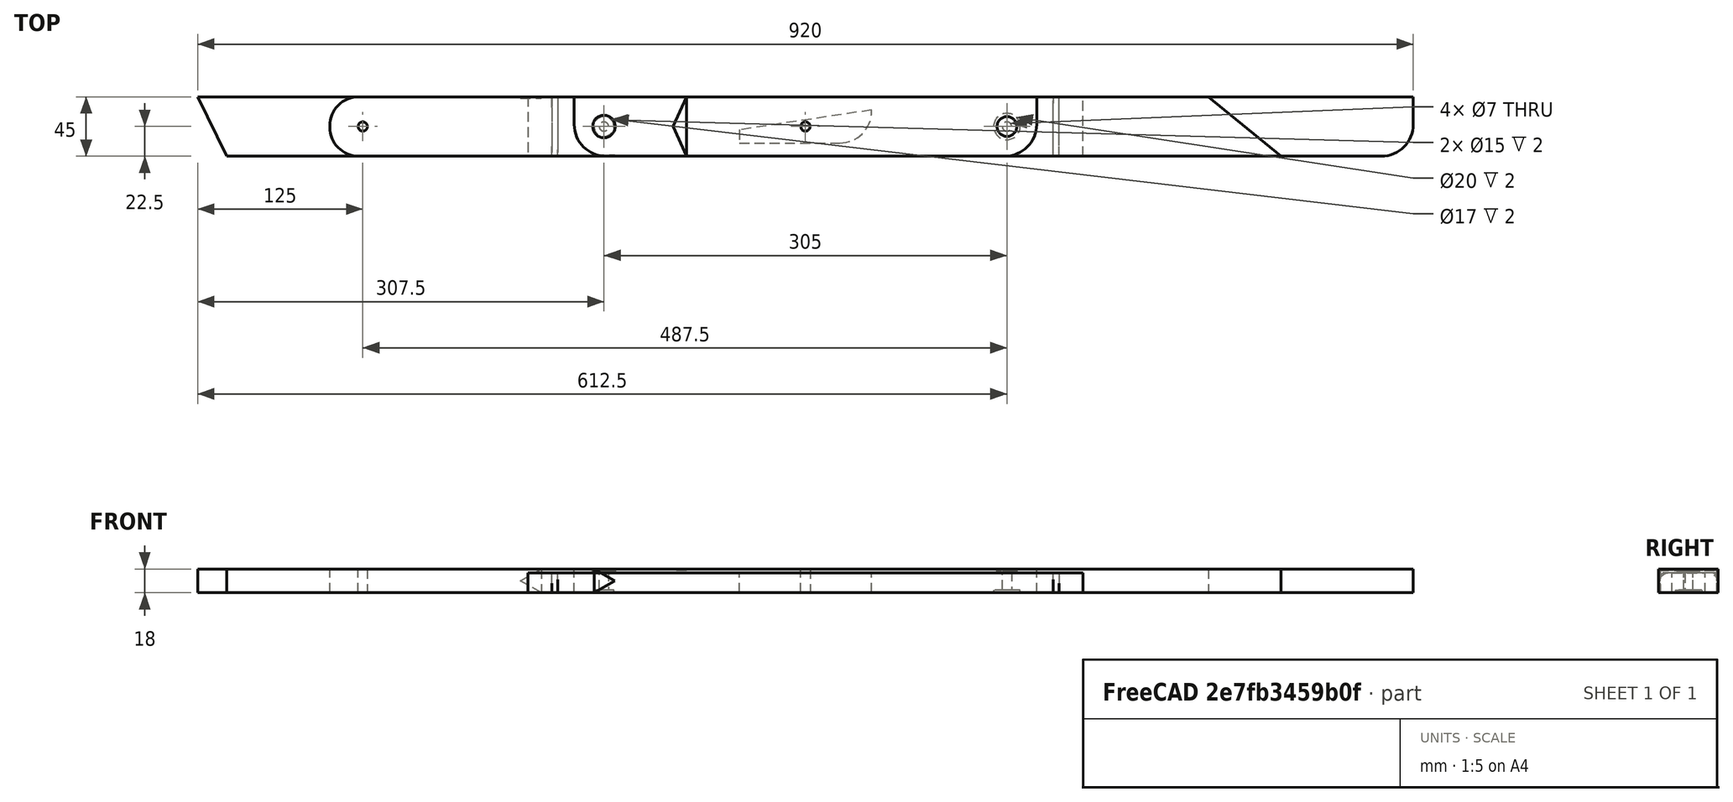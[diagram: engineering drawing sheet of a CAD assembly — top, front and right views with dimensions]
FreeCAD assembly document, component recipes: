
FREECAD ASSEMBLY — COMPONENT RECIPES ("montagem_final")

This assembly document has 20 components, labeled P0..P19 below (a component is one placed body or linked part). 20 of them carry a construction recipe — the FreeCAD feature program that regenerates the part from scratch, quoted from this document or its linked companion documents; the rest are supplied as boundary geometry only. No exploded tour is included for this assembly.
COMPONENT P0 — recipe-attached ("35 X 4,5 X 1,8 (1)", modeled in this document).
Construction recipe (the document's own serialized feature program — sketch geometry with constraints, then the solid features built on it; lengths are millimeters unless a unit is written):

FEATURE [Sketcher::SketchObject] Sketch
  FullyConstrained = true
  MapMode = 5
  Support = -> [XY_Plane]
  sketch-geometry (5):
    g0: LineSegment StartX=-175 StartY=22.5 StartZ=0 EndX=-175 EndY=-22.5 EndZ=0
    g1: LineSegment StartX=-175 StartY=-22.5 StartZ=0 EndX=175 EndY=-22.5 EndZ=0
    g2: LineSegment StartX=175 StartY=-22.5 StartZ=0 EndX=175 EndY=22.5 EndZ=0
    g3: LineSegment StartX=175 StartY=22.5 StartZ=0 EndX=-175 EndY=22.5 EndZ=0
    g4: GeomPoint X=0 Y=0 Z=0
  constraints (12):
    c: Coincident(g0,g1)
    c: Coincident(g1,g2)
    c: Coincident(g2,g3)
    c: Coincident(g3,g0)
    c: Horizontal(g1)
    c: Horizontal(g3)
    c: Vertical(g0)
    c: Vertical(g2)
    c: Symmetric(g1,g0,g4)
    c: Coincident(g4,g-1)
    c: DistanceY(g0,g0) = 45
    c: DistanceX(g3,g3) = 350
FEATURE [PartDesign::Pad] Pad
  Direction = (0,0,1)
  Length = 18
  Length2 = 10
  Profile = -> Sketch
  ReferenceAxis = -> Sketch [N_Axis]
  Type = 0
FEATURE [Sketcher::SketchObject] Sketch001
  ExternalGeometry = -> [Pad]
  FullyConstrained = true
  MapMode = 5
  Placement = pos=(0,0,18) rot=(0,0,1;0rad)
  Support = -> [Pad]
  sketch-geometry (2):
    g0: Circle CenterX=-152.5 CenterY=0 CenterZ=0 NormalX=0 NormalY=0 NormalZ=1 AngleXU=0 Radius=3.5
    g1: Circle CenterX=-152.5 CenterY=0 CenterZ=0 NormalX=0 NormalY=0 NormalZ=1 AngleXU=0 Radius=8.5
  constraints (5):
    c: PointOnObject(g0,g-1)
    c: Diameter(g0) = 7
    c: DistanceX(g-3,g0) = 22.5
    c: Coincident(g1,g0)
    c: Diameter(g1) = 17
FEATURE [PartDesign::Pocket] Pocket
  BaseFeature = -> Pad
  Direction = (0,0,-1)
  Length = 2
  Length2 = 5
  Profile = -> Sketch001
  ReferenceAxis = -> Sketch001 [N_Axis]
  Type = 0
FEATURE [PartDesign::Pocket] Pocket001
  BaseFeature = -> Pocket
  Direction = (0,0,-1)
  Length = 5
  Length2 = 5
  Profile = -> Pocket [Edge18]
  Type = 1
FEATURE [PartDesign::LinearPattern] LinearPattern
  BaseFeature = -> Pocket001
  Direction = -> X_Axis
  Length = 305
  Occurrences = 2
  Originals = -> [Pocket001]
FEATURE [Sketcher::SketchObject] Sketch002
  ExternalGeometry = -> [LinearPattern]
  FullyConstrained = true
  MapMode = 5
  Placement = pos=(0,0,0) rot=(1,0,0;3.14159rad)
  Support = -> [LinearPattern]
  sketch-geometry (1):
    g0: Circle CenterX=152.5 CenterY=0 CenterZ=0 NormalX=0 NormalY=0 NormalZ=1 AngleXU=0 Radius=10
  constraints (2):
    c: Coincident(g0,g-3)
    c: Diameter(g0) = 20
FEATURE [PartDesign::Pocket] Pocket002
  BaseFeature = -> LinearPattern
  Direction = (0,0,1)
  Length = 2
  Length2 = 5
  Profile = -> Sketch002
  ReferenceAxis = -> Sketch002 [N_Axis]
  Type = 0
FEATURE [PartDesign::Fillet] Fillet
  Base = -> Pocket002 [Edge2,Edge8]
  BaseFeature = -> Pocket002
  Radius = 24
  SupportTransform = false
  UseAllEdges = false
FEATURE [Sketcher::SketchObject] Sketch003
  ExternalGeometry = -> [Fillet]
  FullyConstrained = true
  MapMode = 5
  Placement = pos=(0,0,18) rot=(0,0,1;0rad)
  Support = -> [Fillet]
  sketch-geometry (1):
    g0: Circle CenterX=152.5 CenterY=0 CenterZ=0 NormalX=0 NormalY=0 NormalZ=1 AngleXU=0 Radius=7.5
  constraints (2):
    c: Coincident(g0,g-3)
    c: Diameter(g0) = 15
FEATURE [PartDesign::Pocket] Pocket003
  BaseFeature = -> Fillet
  Direction = (0,0,-1)
  Length = 2
  Length2 = 5
  Profile = -> Sketch003
  ReferenceAxis = -> Sketch003 [N_Axis]
  Type = 0
FEATURE [Sketcher::SketchObject] Sketch004
  ExternalGeometry = -> [Pocket003]
  FullyConstrained = true
  MapMode = 5
  Placement = pos=(0,0,0) rot=(1,0,0;3.14159rad)
  Support = -> [Pocket003]
  sketch-geometry (1):
    g0: Circle CenterX=-152.5 CenterY=0 CenterZ=0 NormalX=0 NormalY=0 NormalZ=1 AngleXU=0 Radius=7.5
  constraints (2):
    c: Coincident(g0,g-3)
    c: Diameter(g0) = 15
FEATURE [PartDesign::Pocket] Pocket004
  BaseFeature = -> Pocket003
  Direction = (0,0,1)
  Length = 2
  Length2 = 5
  Profile = -> Sketch004
  ReferenceAxis = -> Sketch004 [N_Axis]
  Type = 0
FEATURE [PartDesign::Body] Body  label="35 x 4,5 x 1,8"
  Group = -> [Sketch,Pad,Sketch001,Pocket,Pocket001,LinearPattern,Sketch002,Pocket002,Fillet,Sketch003,Pocket003,Sketch004,Pocket004]
  Origin = -> Origin
  Tip = -> Pocket004
COMPONENT P1 — recipe-attached ("37,5 X 4,5 X 1,5 (1)", modeled in this document).
Construction recipe (the document's own serialized feature program — sketch geometry with constraints, then the solid features built on it; lengths are millimeters unless a unit is written):

FEATURE [Sketcher::SketchObject] Sketch005
  FullyConstrained = true
  MapMode = 5
  Support = -> [XY_Plane001]
  sketch-geometry (5):
    g0: LineSegment StartX=-187.5 StartY=22.5 StartZ=0 EndX=-187.5 EndY=-22.5 EndZ=0
    g1: LineSegment StartX=-187.5 StartY=-22.5 StartZ=0 EndX=187.5 EndY=-22.5 EndZ=0
    g2: LineSegment StartX=187.5 StartY=-22.5 StartZ=0 EndX=187.5 EndY=22.5 EndZ=0
    g3: LineSegment StartX=187.5 StartY=22.5 StartZ=0 EndX=-187.5 EndY=22.5 EndZ=0
    g4: GeomPoint X=0 Y=0 Z=0
  constraints (12):
    c: Coincident(g0,g1)
    c: Coincident(g1,g2)
    c: Coincident(g2,g3)
    c: Coincident(g3,g0)
    c: Horizontal(g1)
    c: Horizontal(g3)
    c: Vertical(g0)
    c: Vertical(g2)
    c: Symmetric(g1,g0,g4)
    c: Coincident(g4,g-1)
    c: DistanceY(g0,g0) = 45
    c: DistanceX(g3,g3) = 375
FEATURE [PartDesign::Pad] Pad001
  Direction = (0,0,1)
  Length = 15
  Length2 = 10
  Profile = -> Sketch005
  ReferenceAxis = -> Sketch005 [N_Axis]
  Type = 0
FEATURE [PartDesign::Fillet] Fillet001
  Base = -> Pad001 [Edge7,Edge12]
  BaseFeature = -> Pad001
  Radius = 5
  SupportTransform = false
  UseAllEdges = false
FEATURE [PartDesign::Body] Body001  label="37,5 x 4,5 x 1,5"
  Group = -> [Sketch005,Pad001,Fillet001]
  Origin = -> Origin001
  Tip = -> Fillet001
COMPONENT P2 — same part as P1; its construction recipe is shown at P1.
COMPONENT P3 — same part as P0; its construction recipe is shown at P0.
COMPONENT P4 — same part as P1; its construction recipe is shown at P1.
COMPONENT P5 — same part as P1; its construction recipe is shown at P1.
COMPONENT P6 — same part as P1; its construction recipe is shown at P1.
COMPONENT P7 — same part as P1; its construction recipe is shown at P1.
COMPONENT P8 — same part as P1; its construction recipe is shown at P1.
COMPONENT P9 — recipe-attached ("pe1", modeled in this document).
Construction recipe (the document's own serialized feature program — sketch geometry with constraints, then the solid features built on it; lengths are millimeters unless a unit is written):

FEATURE [Sketcher::SketchObject] Sketch006
  FullyConstrained = true
  MapMode = 5
  Support = -> [XY_Plane002]
  sketch-geometry (5):
    g0: LineSegment StartX=-360 StartY=22.5 StartZ=0 EndX=-360 EndY=-22.5 EndZ=0
    g1: LineSegment StartX=-360 StartY=-22.5 StartZ=0 EndX=360 EndY=-22.5 EndZ=0
    g2: LineSegment StartX=360 StartY=-22.5 StartZ=0 EndX=360 EndY=22.5 EndZ=0
    g3: LineSegment StartX=360 StartY=22.5 StartZ=0 EndX=-360 EndY=22.5 EndZ=0
    g4: GeomPoint X=0 Y=0 Z=0
  constraints (12):
    c: Coincident(g0,g1)
    c: Coincident(g1,g2)
    c: Coincident(g2,g3)
    c: Coincident(g3,g0)
    c: Horizontal(g1)
    c: Horizontal(g3)
    c: Vertical(g0)
    c: Vertical(g2)
    c: Symmetric(g1,g0,g4)
    c: Coincident(g4,g-1)
    c: DistanceY(g2,g2) = 45
    c: DistanceX(g3,g3) = 720
FEATURE [PartDesign::Pad] Pad002
  Direction = (0,0,1)
  Length = 18
  Length2 = 10
  Profile = -> Sketch006
  ReferenceAxis = -> Sketch006 [N_Axis]
  Type = 0
FEATURE [Sketcher::SketchObject] Sketch007
  ExternalGeometry = -> [Pad002]
  FullyConstrained = true
  MapMode = 5
  Placement = pos=(0,0,18) rot=(0,0,1;0rad)
  Support = -> [Pad002]
  sketch-geometry (1):
    g0: Circle CenterX=-335 CenterY=0 CenterZ=0 NormalX=0 NormalY=0 NormalZ=1 AngleXU=0 Radius=3.5
  constraints (3):
    c: PointOnObject(g0,g-1)
    c: Diameter(g0) = 7
    c: DistanceX(g-3,g0) = 25
FEATURE [PartDesign::Pocket] Pocket006
  BaseFeature = -> Pad002
  Direction = (0,0,-1)
  Length = 5
  Length2 = 5
  Profile = -> Sketch007
  ReferenceAxis = -> Sketch007 [N_Axis]
  Type = 1
FEATURE [PartDesign::Fillet] Fillet002
  Base = -> Pocket006 [Edge2,Edge1]
  BaseFeature = -> Pocket006
  Radius = 22
  SupportTransform = false
  UseAllEdges = false
FEATURE [Sketcher::SketchObject] Sketch008
  ExternalGeometry = -> [Fillet002]
  FullyConstrained = true
  MapMode = 5
  Placement = pos=(0,0,18) rot=(0,0,1;0rad)
  Support = -> [Fillet002]
  sketch-geometry (3):
    g0: LineSegment StartX=-90 StartY=-22.5 StartZ=0 EndX=-90 EndY=22.5 EndZ=0
    g1: LineSegment StartX=-90 StartY=22.5 StartZ=0 EndX=-100 EndY=0 EndZ=0
    g2: LineSegment StartX=-100 StartY=0 StartZ=0 EndX=-90 EndY=-22.5 EndZ=0
  constraints (9):
    c: PointOnObject(g0,g-3)
    c: PointOnObject(g0,g-4)
    c: Vertical(g0)
    c: Coincident(g0,g1)
    c: PointOnObject(g1,g-1)
    c: Coincident(g1,g2)
    c: Coincident(g2,g0)
    c: DistanceX(g-5,g0) = 270
    c: DistanceX(g1,g0) = 10
FEATURE [PartDesign::Pocket] Pocket007
  BaseFeature = -> Fillet002
  Direction = (0,0,-1)
  Length = 1
  Length2 = 5
  Profile = -> Sketch008
  ReferenceAxis = -> Sketch008 [N_Axis]
  Type = 0
FEATURE [Sketcher::SketchObject] Sketch009
  ExternalGeometry = -> [Pocket007]
  FullyConstrained = true
  MapMode = 5
  Placement = pos=(0,0,18) rot=(0,0,1;0rad)
  Support = -> [Pocket007]
  sketch-geometry (3):
    g0: LineSegment StartX=360 StartY=22.5 StartZ=0 EndX=305 EndY=22.5 EndZ=0
    g1: LineSegment StartX=305 StartY=22.5 StartZ=0 EndX=360 EndY=-22.5 EndZ=0
    g2: LineSegment StartX=360 StartY=22.5 StartZ=0 EndX=360 EndY=-22.5 EndZ=0
  constraints (7):
    c: Coincident(g-4,g0)
    c: PointOnObject(g0,g-3)
    c: Coincident(g0,g1)
    c: Coincident(g1,g-4)
    c: DistanceX(g0,g0) = 55
    c: Coincident(g2,g0)
    c: Coincident(g2,g1)
FEATURE [PartDesign::Pocket] Pocket005
  BaseFeature = -> Pocket007
  Direction = (0,0,-1)
  Length = 5
  Length2 = 5
  Profile = -> Sketch009
  ReferenceAxis = -> Sketch009 [N_Axis]
  Type = 1
FEATURE [PartDesign::Body] Body002  label="72 x 4,5 x 1,8"
  Group = -> [Sketch006,Pad002,Sketch007,Pocket006,Fillet002,Sketch008,Pocket007,Sketch009,Pocket005]
  Origin = -> Origin002
  Tip = -> Pocket005
COMPONENT P10 — same part as P9; its construction recipe is shown at P9.
COMPONENT P11 — same part as P1; its construction recipe is shown at P1.
COMPONENT P12 — recipe-attached ("92 X 4,5 X 1,8 (1)", modeled in this document).
Construction recipe (the document's own serialized feature program — sketch geometry with constraints, then the solid features built on it; lengths are millimeters unless a unit is written):

FEATURE [Sketcher::SketchObject] Sketch010
  FullyConstrained = true
  MapMode = 5
  Support = -> [XY_Plane003]
  sketch-geometry (5):
    g0: LineSegment StartX=-460 StartY=22.5 StartZ=0 EndX=-460 EndY=-22.5 EndZ=0
    g1: LineSegment StartX=-460 StartY=-22.5 StartZ=0 EndX=460 EndY=-22.5 EndZ=0
    g2: LineSegment StartX=460 StartY=-22.5 StartZ=0 EndX=460 EndY=22.5 EndZ=0
    g3: LineSegment StartX=460 StartY=22.5 StartZ=0 EndX=-460 EndY=22.5 EndZ=0
    g4: GeomPoint X=0 Y=0 Z=0
  constraints (12):
    c: Coincident(g0,g1)
    c: Coincident(g1,g2)
    c: Coincident(g2,g3)
    c: Coincident(g3,g0)
    c: Horizontal(g1)
    c: Horizontal(g3)
    c: Vertical(g0)
    c: Vertical(g2)
    c: Symmetric(g1,g0,g4)
    c: Coincident(g4,g-1)
    c: DistanceY(g2,g2) = 45
    c: DistanceX(g3,g3) = 920
FEATURE [PartDesign::Pad] Pad003
  Direction = (0,0,1)
  Length = 18
  Length2 = 10
  Profile = -> Sketch010
  ReferenceAxis = -> Sketch010 [N_Axis]
  Type = 0
FEATURE [Sketcher::SketchObject] Sketch011
  FullyConstrained = true
  MapMode = 5
  Placement = pos=(0,0,18) rot=(0,0,1;0rad)
  Support = -> [Pad003]
  sketch-geometry (1):
    g0: Circle CenterX=0 CenterY=0 CenterZ=0 NormalX=0 NormalY=0 NormalZ=1 AngleXU=0 Radius=3.5
  constraints (2):
    c: Coincident(g0,g-1)
    c: Diameter(g0) = 7
FEATURE [PartDesign::Pocket] Pocket009
  BaseFeature = -> Pad003
  Direction = (0,0,-1)
  Length = 5
  Length2 = 5
  Profile = -> Sketch011
  ReferenceAxis = -> Sketch011 [N_Axis]
  Type = 1
FEATURE [PartDesign::Fillet] Fillet003
  Base = -> Pocket009 [Edge8]
  BaseFeature = -> Pocket009
  Radius = 24
  SupportTransform = false
  UseAllEdges = false
FEATURE [Sketcher::SketchObject] Sketch012
  ExternalGeometry = -> [Fillet003]
  FullyConstrained = true
  MapMode = 5
  Placement = pos=(0,-22.5,0) rot=(1,0,0;1.5708rad)
  Support = -> [Fillet003]
  sketch-geometry (3):
    g0: LineSegment StartX=-160 StartY=18 StartZ=0 EndX=-160 EndY=0 EndZ=0
    g1: LineSegment StartX=-160 StartY=0 StartZ=0 EndX=-144.412 EndY=9 EndZ=0
    g2: LineSegment StartX=-144.412 StartY=9 StartZ=0 EndX=-160 EndY=18 EndZ=0
  constraints (9):
    c: PointOnObject(g0,g-3)
    c: PointOnObject(g0,g-4)
    c: Vertical(g0)
    c: DistanceX(g-3,g0) = 300
    c: Coincident(g0,g1)
    c: Coincident(g1,g2)
    c: Coincident(g2,g0)
    c: Equal(g2,g1)
    c: Equal(g0,g1)
FEATURE [PartDesign::Pocket] Pocket010
  BaseFeature = -> Fillet003
  Direction = (0,1,-2e-16)
  Length = 1
  Length2 = 5
  Profile = -> Sketch012
  ReferenceAxis = -> Sketch012 [N_Axis]
  Type = 0
FEATURE [Sketcher::SketchObject] Sketch013
  ExternalGeometry = -> [Pocket010]
  FullyConstrained = true
  MapMode = 5
  Placement = pos=(0,22.5,0) rot=(0,0.707107,0.707107;3.14159rad)
  Support = -> [Pocket010]
  sketch-geometry (3):
    g0: LineSegment StartX=200 StartY=18 StartZ=0 EndX=200 EndY=0 EndZ=0
    g1: LineSegment StartX=200 StartY=0 StartZ=0 EndX=215.588 EndY=9 EndZ=0
    g2: LineSegment StartX=215.588 StartY=9 StartZ=0 EndX=200 EndY=18 EndZ=0
  constraints (9):
    c: PointOnObject(g0,g-3)
    c: PointOnObject(g0,g-4)
    c: Vertical(g0)
    c: Coincident(g0,g1)
    c: Coincident(g1,g2)
    c: Coincident(g2,g0)
    c: Equal(g0,g2)
    c: Equal(g2,g1)
    c: DistanceX(g0,g-3) = 260
FEATURE [PartDesign::Pocket] Pocket011
  BaseFeature = -> Pocket010
  Direction = (0,-1,2e-16)
  Length = 1
  Length2 = 5
  Profile = -> Sketch013
  ReferenceAxis = -> Sketch013 [N_Axis]
  Type = 0
FEATURE [Sketcher::SketchObject] Sketch014
  ExternalGeometry = -> [Pocket011]
  FullyConstrained = true
  MapMode = 5
  Placement = pos=(0,0,18) rot=(0,0,1;0rad)
  Support = -> [Pocket011]
  sketch-geometry (3):
    g0: LineSegment StartX=-460 StartY=-22.5 StartZ=0 EndX=-438 EndY=-22.5 EndZ=0
    g1: LineSegment StartX=-438 StartY=-22.5 StartZ=0 EndX=-460 EndY=22.5 EndZ=0
    g2: LineSegment StartX=-460 StartY=22.5 StartZ=0 EndX=-460 EndY=-22.5 EndZ=0
  constraints (7):
    c: Coincident(g-3,g0)
    c: PointOnObject(g0,g-3)
    c: Coincident(g0,g1)
    c: Coincident(g1,g-4)
    c: Coincident(g1,g2)
    c: Coincident(g2,g0)
    c: DistanceX(g0,g0) = 22
FEATURE [PartDesign::Pocket] Pocket008
  BaseFeature = -> Pocket011
  Direction = (0,0,-1)
  Length = 5
  Length2 = 5
  Profile = -> Sketch014
  ReferenceAxis = -> Sketch014 [N_Axis]
  Type = 1
FEATURE [PartDesign::Body] Body003  label="92 x 4,5 x 1,8"
  Group = -> [Sketch010,Pad003,Sketch011,Pocket009,Fillet003,Sketch012,Pocket010,Sketch013,Pocket011,Sketch014,Pocket008]
  Origin = -> Origin003
  Tip = -> Pocket008
COMPONENT P13 — recipe-attached ("42 X 4,5 X 1,5 (1)", modeled in this document).
Construction recipe (the document's own serialized feature program — sketch geometry with constraints, then the solid features built on it; lengths are millimeters unless a unit is written):

FEATURE [Sketcher::SketchObject] Sketch015
  FullyConstrained = true
  MapMode = 5
  Support = -> [XY_Plane004]
  sketch-geometry (5):
    g0: LineSegment StartX=-210 StartY=22.5 StartZ=0 EndX=-210 EndY=-22.5 EndZ=0
    g1: LineSegment StartX=-210 StartY=-22.5 StartZ=0 EndX=210 EndY=-22.5 EndZ=0
    g2: LineSegment StartX=210 StartY=-22.5 StartZ=0 EndX=210 EndY=22.5 EndZ=0
    g3: LineSegment StartX=210 StartY=22.5 StartZ=0 EndX=-210 EndY=22.5 EndZ=0
    g4: GeomPoint X=0 Y=0 Z=0
  constraints (12):
    c: Coincident(g0,g1)
    c: Coincident(g1,g2)
    c: Coincident(g2,g3)
    c: Coincident(g3,g0)
    c: Horizontal(g1)
    c: Horizontal(g3)
    c: Vertical(g0)
    c: Vertical(g2)
    c: Symmetric(g1,g0,g4)
    c: Coincident(g4,g-1)
    c: DistanceY(g0,g0) = 45
    c: DistanceX(g3,g3) = 420
FEATURE [PartDesign::Pad] Pad004
  Direction = (0,0,1)
  Length = 15
  Length2 = 10
  Profile = -> Sketch015
  ReferenceAxis = -> Sketch015 [N_Axis]
  Type = 0
FEATURE [PartDesign::Body] Body004  label="42 x 4,5 x 1,5"
  Group = -> [Sketch015,Pad004]
  Origin = -> Origin004
  Tip = -> Pad004
COMPONENT P14 — same part as P12; its construction recipe is shown at P12.
COMPONENT P15 — same part as P13; its construction recipe is shown at P13.
COMPONENT P16 — recipe-attached ("p7 (1)", modeled in this document).
Construction recipe (the document's own serialized feature program — sketch geometry with constraints, then the solid features built on it; lengths are millimeters unless a unit is written):

FEATURE [Sketcher::SketchObject] Sketch016
  FullyConstrained = true
  MapMode = 5
  Support = -> [XY_Plane005]
  sketch-geometry (5):
    g0: LineSegment StartX=-50 StartY=12.5 StartZ=0 EndX=-50 EndY=-12.5 EndZ=0
    g1: LineSegment StartX=-50 StartY=-12.5 StartZ=0 EndX=50 EndY=-12.5 EndZ=0
    g2: LineSegment StartX=50 StartY=-12.5 StartZ=0 EndX=50 EndY=12.5 EndZ=0
    g3: LineSegment StartX=50 StartY=12.5 StartZ=0 EndX=-50 EndY=12.5 EndZ=0
    g4: GeomPoint X=0 Y=0 Z=0
  constraints (12):
    c: Coincident(g0,g1)
    c: Coincident(g1,g2)
    c: Coincident(g2,g3)
    c: Coincident(g3,g0)
    c: Horizontal(g1)
    c: Horizontal(g3)
    c: Vertical(g0)
    c: Vertical(g2)
    c: Symmetric(g1,g0,g4)
    c: Coincident(g4,g-1)
    c: DistanceX(g3,g3) = 100
    c: DistanceY(g0,g0) = 25
FEATURE [PartDesign::Pad] Pad005
  Direction = (0,0,1)
  Length = 15
  Length2 = 10
  Profile = -> Sketch016
  ReferenceAxis = -> Sketch016 [N_Axis]
  Type = 0
FEATURE [PartDesign::Fillet] Fillet004
  Base = -> Pad005 [Edge5]
  BaseFeature = -> Pad005
  Radius = 24
  SupportTransform = false
  UseAllEdges = false
FEATURE [Sketcher::SketchObject] Sketch017
  ExternalGeometry = -> [Fillet004]
  FullyConstrained = true
  MapMode = 5
  Placement = pos=(0,0,15) rot=(0,0,1;0rad)
  Support = -> [Fillet004]
  sketch-geometry (3):
    g0: LineSegment StartX=50 StartY=12.5 StartZ=0 EndX=-50 EndY=-2.5 EndZ=0
    g1: LineSegment StartX=-50 StartY=-2.5 StartZ=0 EndX=-50 EndY=12.5 EndZ=0
    g2: LineSegment StartX=-50 StartY=12.5 StartZ=0 EndX=50 EndY=12.5 EndZ=0
  constraints (7):
    c: Coincident(g-3,g0)
    c: Coincident(g0,g1)
    c: Coincident(g1,g-3)
    c: Vertical(g1)
    c: Coincident(g1,g2)
    c: Coincident(g2,g0)
    c: DistanceY(g1,g1) = 15
FEATURE [PartDesign::Pocket] Pocket012
  BaseFeature = -> Fillet004
  Direction = (0,0,-1)
  Length = 5
  Length2 = 5
  Profile = -> Sketch017
  ReferenceAxis = -> Sketch017 [N_Axis]
  Type = 1
FEATURE [PartDesign::Body] Body005  label="Anteparo"
  Group = -> [Sketch016,Pad005,Fillet004,Sketch017,Pocket012]
  Origin = -> Origin005
  Tip = -> Pocket012
COMPONENT P17 — same part as P16; its construction recipe is shown at P16.
COMPONENT P18 — recipe-attached ("38,4 X 4,5 X 1,5 (1)", modeled in this document).
Construction recipe (the document's own serialized feature program — sketch geometry with constraints, then the solid features built on it; lengths are millimeters unless a unit is written):

FEATURE [Sketcher::SketchObject] Sketch018
  FullyConstrained = true
  MapMode = 5
  Support = -> [XY_Plane006]
  sketch-geometry (5):
    g0: LineSegment StartX=-192 StartY=22.5 StartZ=0 EndX=-192 EndY=-22.5 EndZ=0
    g1: LineSegment StartX=-192 StartY=-22.5 StartZ=0 EndX=192 EndY=-22.5 EndZ=0
    g2: LineSegment StartX=192 StartY=-22.5 StartZ=0 EndX=192 EndY=22.5 EndZ=0
    g3: LineSegment StartX=192 StartY=22.5 StartZ=0 EndX=-192 EndY=22.5 EndZ=0
    g4: GeomPoint X=0 Y=0 Z=0
  constraints (12):
    c: Coincident(g0,g1)
    c: Coincident(g1,g2)
    c: Coincident(g2,g3)
    c: Coincident(g3,g0)
    c: Horizontal(g1)
    c: Horizontal(g3)
    c: Vertical(g0)
    c: Vertical(g2)
    c: Symmetric(g1,g0,g4)
    c: Coincident(g4,g-1)
    c: DistanceY(g0,g0) = 45
    c: DistanceX(g3,g3) = 384
FEATURE [PartDesign::Pad] Pad006
  Direction = (0,0,1)
  Length = 15
  Length2 = 10
  Profile = -> Sketch018
  ReferenceAxis = -> Sketch018 [N_Axis]
  Type = 0
FEATURE [PartDesign::Fillet] Fillet006
  Base = -> Pad006 [Edge7]
  BaseFeature = -> Pad006
  Radius = 8
  SupportTransform = false
  UseAllEdges = false
FEATURE [PartDesign::Fillet] Fillet005
  Base = -> Fillet006 [Edge13]
  BaseFeature = -> Fillet006
  Radius = 8
  SupportTransform = false
  UseAllEdges = false
FEATURE [PartDesign::Body] Body006  label="38,4 X 4,5 X 1,5"
  Group = -> [Sketch018,Pad006,Fillet006,Fillet005]
  Origin = -> Origin006
  Tip = -> Fillet005
COMPONENT P19 — same part as P18; its construction recipe is shown at P18.
PROVENANCE & LICENSES
A FreeCAD (.FCStd) document from a public repository crawl; recipes are the document's own serialized feature recipes (and, for linked parts, companion documents' recipes).
License: as declared in the source repository (recorded in the dataset sidecar).
